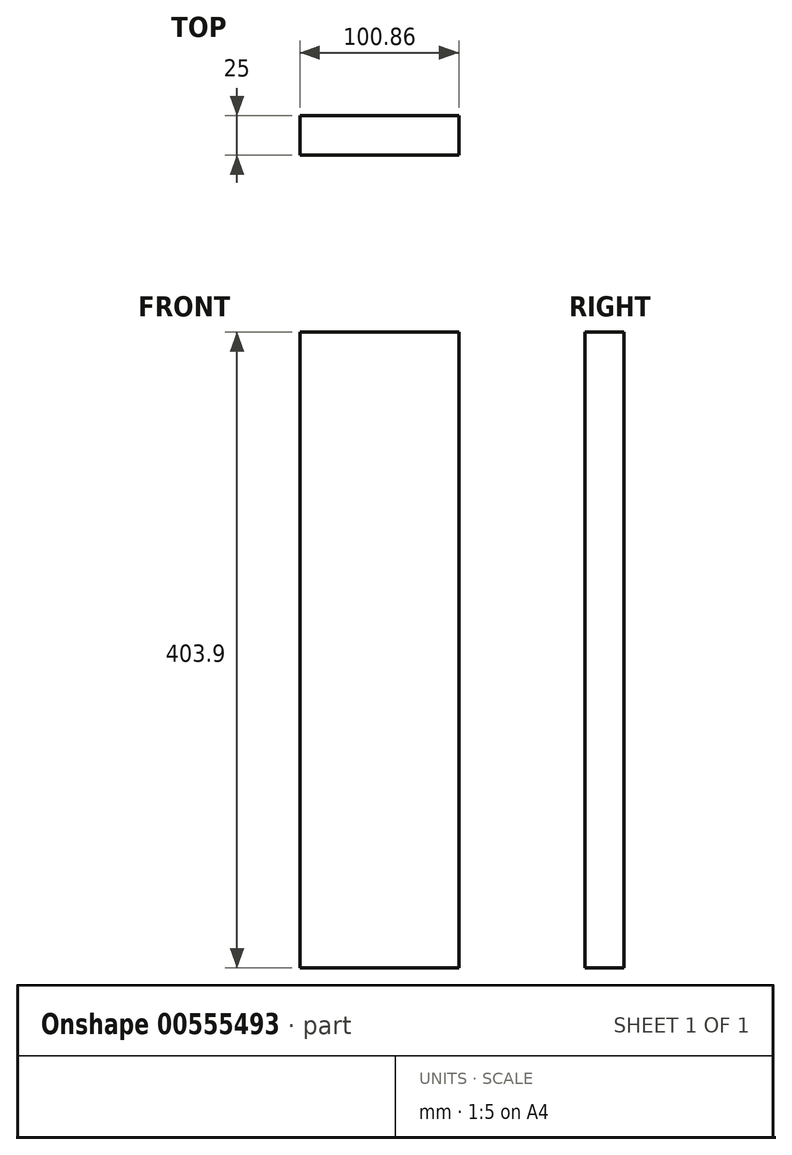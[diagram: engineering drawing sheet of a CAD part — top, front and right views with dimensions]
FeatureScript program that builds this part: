
annotation { "Feature Type Name" : "Feature", "Feature Type Description" : "" }
export const myFeature = defineFeature(function(context is Context, id is Id, definition is map)
    precondition{}
    {
        {
            var Q0;
            Q0=qCreatedBy(makeId("Front.planeOp"),FACE);
            var sketch = newSketch(context, id + "F0", { "sketchPlane" : qUnion([Q0])});
            skLineSegment(sketch, "E0", {"start": v(-593.29, 91.36) * mm, "end": v(606.71, 91.36) * mm});
            skLineSegment(sketch, "E1", {"start": v(-593.29, 91.36) * mm, "end": v(-593.29, -312.54) * mm});
            skLineSegment(sketch, "E2", {"start": v(-593.29, -312.54) * mm, "end": v(606.71, -312.54) * mm});
            skLineSegment(sketch, "E3", {"start": v(606.71, -312.54) * mm, "end": v(606.71, 91.36) * mm});
            skSolve(sketch);
        }
        {
            var Q0;
            Q0 = qSketchRegion(id + "F0", true);
            extrude(context, id + "F1", {"entities" : qUnion([Q0]), "depth" : 25 * mm, "offsetDistance" : 25 * mm});
        }
        {
            var Q0;
            Q0=makeQuery(id+"F1.opExtrude","CAP_FACE",FACE,{"disambiguationData":[OSD([sQuery(id+"F0.wireOp",EDGE,"E0"),sQuery(id+"F0.wireOp",EDGE,"E1"),sQuery(id+"F0.wireOp",EDGE,"E2"),sQuery(id+"F0.wireOp",EDGE,"E3")])],"isStart":false});
            var sketch = newSketch(context, id + "F2", { "sketchPlane" : qUnion([Q0])});
            skCircle(sketch, "E4", {"center": v(-540.35, 67.86) * mm, "radius": 12.5 * mm});
            skCircle(sketch, "E5", {"center": v(-540.35, -289.04) * mm, "radius": 12.5 * mm});
            skCircle(sketch, "E6", {"center": v(59.12, 67.86) * mm, "radius": 12.5 * mm});
            skCircle(sketch, "E7", {"center": v(59.12, -289.04) * mm, "radius": 12.5 * mm});
            skCircle(sketch, "E8", {"center": v(553.77, 67.86) * mm, "radius": 12.5 * mm});
            skCircle(sketch, "E9", {"center": v(553.77, -289.04) * mm, "radius": 12.5 * mm});
            skSolve(sketch);
        }
        {
            var Q0;
            Q0 = qSketchRegion(id + "F2", true);
            extrude(context, id + "F3", {"entities" : qUnion([Q0]), "operationType" : NewBodyOperationType.REMOVE, "oppositeDirection" : true, "depth" : 25 * mm, "offsetDistance" : 25 * mm});
        }
        {
            var Q0;
            Q0=makeQuery(id+"F1.opExtrude","CAP_FACE",FACE,{"disambiguationData":[OSD([sQuery(id+"F0.wireOp",EDGE,"E0"),sQuery(id+"F0.wireOp",EDGE,"E1"),sQuery(id+"F0.wireOp",EDGE,"E2"),sQuery(id+"F0.wireOp",EDGE,"E3")])],"isStart":true});
            var sketch = newSketch(context, id + "F4", { "sketchPlane" : qUnion([Q0])});
            skCircle(sketch, "E10", {"center": v(466.9, 67.71) * mm, "radius": 10.96 * mm});
            skSolve(sketch);
        }
        {
            var Q0;
            Q0 = qSketchRegion(id + "F4", true);
            extrude(context, id + "F5", {"entities" : qUnion([Q0]), "operationType" : NewBodyOperationType.REMOVE, "oppositeDirection" : true, "depth" : 25 * mm, "offsetDistance" : 25 * mm});
        }
        {
            var Q0;
            Q0=makeQuery(id+"F1.opExtrude","CAP_FACE",FACE,{"disambiguationData":[OSD([sQuery(id+"F0.wireOp",EDGE,"E0"),sQuery(id+"F0.wireOp",EDGE,"E1"),sQuery(id+"F0.wireOp",EDGE,"E2"),sQuery(id+"F0.wireOp",EDGE,"E3")])],"isStart":true});
            var sketch = newSketch(context, id + "F6", { "sketchPlane" : qUnion([Q0])});
            skLineSegment(sketch, "E11", {"start": v(501.57, -312.54) * mm, "end": v(501.57, 91.36) * mm});
            skLineSegment(sketch, "E12", {"start": v(384.72, -312.54) * mm, "end": v(384.72, 91.36) * mm});
            skLineSegment(sketch, "E13", {"start": v(277.1, -312.54) * mm, "end": v(277.1, 91.36) * mm});
            skLineSegment(sketch, "E14", {"start": v(151.03, -312.54) * mm, "end": v(151.03, 91.36) * mm});
            skLineSegment(sketch, "E15", {"start": v(49.56, -312.54) * mm, "end": v(49.56, 91.36) * mm});
            skLineSegment(sketch, "E16", {"start": v(-74.98, -312.54) * mm, "end": v(-74.98, 91.36) * mm});
            skLineSegment(sketch, "E17", {"start": v(-170.3, -312.54) * mm, "end": v(-170.3, 91.36) * mm});
            skLineSegment(sketch, "E18", {"start": v(-297.9, -312.54) * mm, "end": v(-297.9, 91.36) * mm});
            skLineSegment(sketch, "E19", {"start": v(-394.77, -312.54) * mm, "end": v(-394.77, 91.36) * mm});
            skLineSegment(sketch, "E20", {"start": v(-503.93, -312.54) * mm, "end": v(-503.93, 91.36) * mm});
            skSolve(sketch);
        }
        {
            var Q0;
            Q0 = qSketchRegion(id + "F6", true);
            var Q1;
            {var subQ0=sQuery(id+"F6.wireOp",EDGE,"E11");Q1=makeQuery(id+"F6.imprint","IMPRINT",FACE,{"disambiguationData":[TD([[makeQuery(id+"F6.imprint","IMPRINT",EDGE,{"derivedFrom":subQ0}),1.0]])]});}
            var Q2;
            {var subQ15=makeQuery(id+"F1.opExtrude","CAP_EDGE",EDGE,{"disambiguationData":[OSD([sQuery(id+"F0.wireOp",EDGE,"E3")])],"isStart":true});Q2=makeQuery(id+"F6.imprint","IMPRINT",FACE,{"disambiguationData":[TD([[makeQuery(id+"F6.imprint","IMPRINT",EDGE,{"derivedFrom":subQ15}),-1.0]])]});}
            var Q3;
            {var subQ7=sQuery(id+"F6.wireOp",EDGE,"E19");Q3=makeQuery(id+"F6.imprint","IMPRINT",FACE,{"disambiguationData":[TD([[makeQuery(id+"F6.imprint","IMPRINT",EDGE,{"derivedFrom":subQ7}),1.0]])]});}
            var Q4;
            {var subQ1=sQuery(id+"F6.wireOp",EDGE,"E17");Q4=makeQuery(id+"F6.imprint","IMPRINT",FACE,{"disambiguationData":[TD([[makeQuery(id+"F6.imprint","IMPRINT",EDGE,{"derivedFrom":subQ1}),1.0]])]});}
            var Q5;
            {var subQ0=sQuery(id+"F6.wireOp",EDGE,"E16");Q5=makeQuery(id+"F6.imprint","IMPRINT",FACE,{"disambiguationData":[TD([[makeQuery(id+"F6.imprint","IMPRINT",EDGE,{"derivedFrom":subQ0}),1.0]])]});}
            var Q6;
            {var subQ0=sQuery(id+"F6.wireOp",EDGE,"E15");Q6=makeQuery(id+"F6.imprint","IMPRINT",FACE,{"disambiguationData":[TD([[makeQuery(id+"F6.imprint","IMPRINT",EDGE,{"derivedFrom":subQ0}),1.0]])]});}
            var Q7;
            {var subQ0=sQuery(id+"F6.wireOp",EDGE,"E14");Q7=makeQuery(id+"F6.imprint","IMPRINT",FACE,{"disambiguationData":[TD([[makeQuery(id+"F6.imprint","IMPRINT",EDGE,{"derivedFrom":subQ0}),1.0]])]});}
            var Q8;
            {var subQ1=sQuery(id+"F6.wireOp",EDGE,"E13");Q8=makeQuery(id+"F6.imprint","IMPRINT",FACE,{"disambiguationData":[TD([[makeQuery(id+"F6.imprint","IMPRINT",EDGE,{"derivedFrom":subQ1}),1.0]])]});}
            var Q9;
            {var subQ0=sQuery(id+"F6.wireOp",EDGE,"E12");Q9=makeQuery(id+"F6.imprint","IMPRINT",FACE,{"disambiguationData":[TD([[makeQuery(id+"F6.imprint","IMPRINT",EDGE,{"derivedFrom":subQ0}),1.0]])]});}
            var Q10;
            {var subQ2=sQuery(id+"F6.wireOp",EDGE,"E11");Q10=makeQuery(id+"F6.imprint","IMPRINT",FACE,{"disambiguationData":[TD([[makeQuery(id+"F6.imprint","IMPRINT",EDGE,{"derivedFrom":subQ2}),-1.0]])]});}
            extrude(context, id + "F7", {"entities" : qUnion([Q0, Q1, Q2, Q3, Q4, Q5, Q6, Q7, Q8, Q9, Q10]), "operationType" : NewBodyOperationType.REMOVE, "oppositeDirection" : true, "depth" : 25 * mm, "offsetDistance" : 25 * mm});
        }
        {
            var Q0;
            Q0=makeQuery(id+"F7.boolean.opBoolean","COPY",FACE,{"derivedFrom":makeQuery(id+"F7.opExtrude","SWEPT_FACE",FACE,{"disambiguationData":[OSD([sQuery(id+"F6.wireOp",EDGE,"E18")])]})});
            extrude(context, id + "F8", {"entities" : qUnion([Q0]), "operationType" : NewBodyOperationType.ADD, "depth" : 4 * mm, "offsetDistance" : 25 * mm});
        }
        {
            var Q0;
            {var subQ0=sQuery(id+"F6.wireOp",EDGE,"E18");Q0=makeQuery(id+"F8.boolean.opBoolean","MERGE",FACE,{"derivedFrom":[makeQuery(id+"F1.opExtrude","CAP_FACE",FACE,{"disambiguationData":[OSD([sQuery(id+"F0.wireOp",EDGE,"E0"),sQuery(id+"F0.wireOp",EDGE,"E1"),sQuery(id+"F0.wireOp",EDGE,"E2"),sQuery(id+"F0.wireOp",EDGE,"E3")])],"isStart":true}),makeQuery(id+"F8.opExtrude","SWEPT_FACE",FACE,{"disambiguationData":[OSD([subQ0]),TDD([makeQuery(id+"F7.boolean.opBoolean","COPY",EDGE,{"derivedFrom":makeQuery(id+"F7.opExtrude","CAP_EDGE",EDGE,{"disambiguationData":[OSD([subQ0])],"isStart":true})})])]})]});}
            var sketch = newSketch(context, id + "F9", { "sketchPlane" : qUnion([Q0])});
            skCircle(sketch, "E21", {"center": v(-344.34, 69.36) * mm, "radius": 11 * mm});
            skPoint(sketch, "E21.centerSnap0", {"position": v(-344.34, 91.36) * mm});
            skCircle(sketch, "E22", {"center": v(-344.34, -289.15) * mm, "radius": 12.4 * mm});
            skPoint(sketch, "E22.centerSnap0", {"position": v(-344.34, -312.54) * mm});
            skSolve(sketch);
        }
        {
            var Q0;
            Q0 = qSketchRegion(id + "F9", true);
            extrude(context, id + "F10", {"entities" : qUnion([Q0]), "operationType" : NewBodyOperationType.REMOVE, "oppositeDirection" : true, "depth" : 25 * mm, "offsetDistance" : 25 * mm});
        }
        {
            var Q0;
            {var subQ0=sQuery(id+"F6.wireOp",EDGE,"E18");Q0=makeQuery(id+"F8.boolean.opBoolean","MERGE",FACE,{"derivedFrom":[makeQuery(id+"F1.opExtrude","CAP_FACE",FACE,{"disambiguationData":[OSD([sQuery(id+"F0.wireOp",EDGE,"E0"),sQuery(id+"F0.wireOp",EDGE,"E1"),sQuery(id+"F0.wireOp",EDGE,"E2"),sQuery(id+"F0.wireOp",EDGE,"E3")])],"isStart":true}),makeQuery(id+"F8.opExtrude","SWEPT_FACE",FACE,{"disambiguationData":[OSD([subQ0]),TDD([makeQuery(id+"F7.boolean.opBoolean","COPY",EDGE,{"derivedFrom":makeQuery(id+"F7.opExtrude","CAP_EDGE",EDGE,{"disambiguationData":[OSD([subQ0])],"isStart":true})})])]})]});}
            var sketch = newSketch(context, id + "F11", { "sketchPlane" : qUnion([Q0])});
            skLineSegment(sketch, "E23", {"start": v(-394.77, 34.02) * mm, "end": v(-293.9, 34.02) * mm});
            skLineSegment(sketch, "E24", {"start": v(-293.9, 34.02) * mm, "end": v(-293.9, 17.92) * mm});
            skLineSegment(sketch, "E25", {"start": v(-293.9, 17.92) * mm, "end": v(-394.77, 17.92) * mm});
            skLineSegment(sketch, "E26", {"start": v(-394.77, 17.92) * mm, "end": v(-394.77, 34.02) * mm});
            skLineSegment(sketch, "E27", {"start": v(-293.9, -259.4) * mm, "end": v(-394.77, -259.4) * mm});
            skLineSegment(sketch, "E28", {"start": v(-394.77, -259.4) * mm, "end": v(-394.77, -243.3) * mm});
            skLineSegment(sketch, "E29", {"start": v(-394.77, -243.3) * mm, "end": v(-293.9, -243.3) * mm});
            skLineSegment(sketch, "E30", {"start": v(-293.9, -243.3) * mm, "end": v(-293.9, -259.4) * mm});
            skSolve(sketch);
        }
        {
            var Q0;
            Q0 = qSketchRegion(id + "F11", true);
            extrude(context, id + "F12", {"entities" : qUnion([Q0]), "operationType" : NewBodyOperationType.REMOVE, "oppositeDirection" : true, "depth" : 22 * mm, "offsetDistance" : 25 * mm});
        }
    });
